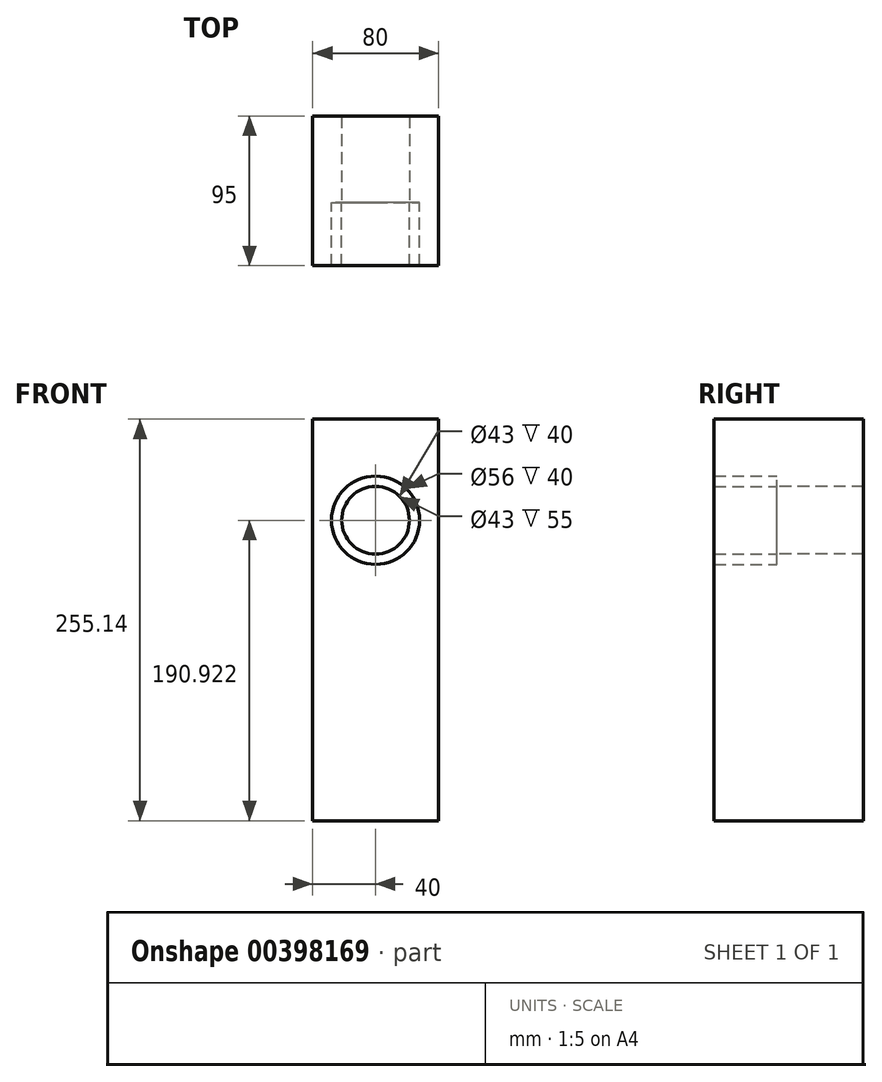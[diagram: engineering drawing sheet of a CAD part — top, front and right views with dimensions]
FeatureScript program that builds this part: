
annotation { "Feature Type Name" : "Feature", "Feature Type Description" : "" }
export const myFeature = defineFeature(function(context is Context, id is Id, definition is map)
    precondition{}
    {
        {
            var Q0;
            Q0=qCreatedBy(makeId("Front.planeOp"),FACE);
            var sketch = newSketch(context, id + "F0", { "sketchPlane" : qUnion([Q0])});
            skLineSegment(sketch, "E0.bottom", {"start": v(40, -127.57) * mm, "end": v(-40, -127.57) * mm});
            skLineSegment(sketch, "E0.top", {"start": v(40, 127.57) * mm, "end": v(-40, 127.57) * mm});
            skLineSegment(sketch, "E0.left", {"start": v(40, -127.57) * mm, "end": v(40, 127.57) * mm});
            skLineSegment(sketch, "E0.right", {"start": v(-40, -127.57) * mm, "end": v(-40, 127.57) * mm});
            skPoint(sketch, "E0.middle", {"position": v(0, 0) * mm});
            skSolve(sketch);
        }
        {
            var Q0;
            Q0=qSketchRegion(id+"F0",true);
            extrude(context, id + "F1", {"entities" : qUnion([Q0]), "depth" : 95 * mm});
        }
        {
            var Q0;
            Q0=makeQuery(id+"F1.opExtrude","CAP_FACE",FACE,{"disambiguationData":[OSD([sQuery(id+"F0.wireOp",EDGE,"E0.bottom"),sQuery(id+"F0.wireOp",EDGE,"E0.top"),sQuery(id+"F0.wireOp",EDGE,"E0.left"),sQuery(id+"F0.wireOp",EDGE,"E0.right")])],"isStart":false});
            var sketch = newSketch(context, id + "F2", { "sketchPlane" : qUnion([Q0])});
            skCircle(sketch, "E1", {"center": v(0, 63.35) * mm, "radius": 28 * mm});
            skSolve(sketch);
        }
        {
            var Q0;
            Q0=qSketchRegion(id+"F2",true);
            extrude(context, id + "F3", {"entities" : qUnion([Q0]), "operationType" : NewBodyOperationType.REMOVE, "oppositeDirection" : true, "depth" : 40 * mm});
        }
        {
            var Q0;
            Q0=makeQuery(id+"F3.boolean.opBoolean","COPY",FACE,{"derivedFrom":makeQuery(id+"F3.opExtrude","CAP_FACE",FACE,{"disambiguationData":[OSD([sQuery(id+"F2.wireOp",EDGE,"E1")])],"isStart":false})});
            var sketch = newSketch(context, id + "F4", { "sketchPlane" : qUnion([Q0])});
            skCircle(sketch, "E2", {"center": v(0, 63.35) * mm, "radius": 21.5 * mm});
            skSolve(sketch);
        }
        {
            var Q0;
            Q0=qSketchRegion(id+"F4",true);
            extrude(context, id + "F5", {"entities" : qUnion([Q0]), "operationType" : NewBodyOperationType.REMOVE, "endBound" : BoundingType.THROUGH_ALL, "oppositeDirection" : true, "depth" : 25 * mm});
        }
        {
            var Q0;
            Q0=makeQuery(id+"F3.boolean.opBoolean","COPY",FACE,{"derivedFrom":makeQuery(id+"F3.opExtrude","CAP_FACE",FACE,{"disambiguationData":[OSD([sQuery(id+"F2.wireOp",EDGE,"E1")])],"isStart":false})});
            var sketch = newSketch(context, id + "F6", { "sketchPlane" : qUnion([Q0])});
            skCircle(sketch, "E3", {"center": v(0, 63.35) * mm, "radius": 28 * mm});
            skCircle(sketch, "E4", {"center": v(0, 63.35) * mm, "radius": 21.5 * mm});
            skSolve(sketch);
        }
        {
            var Q0;
            Q0=qSketchRegion(id+"F6",true);
            extrude(context, id + "F7", {"entities" : qUnion([Q0]), "depth" : 40 * mm});
        }
    });
